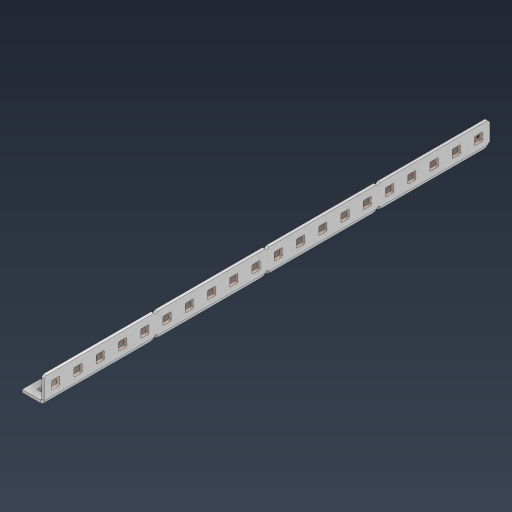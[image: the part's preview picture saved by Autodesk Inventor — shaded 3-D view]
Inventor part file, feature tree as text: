
AUTODESK INVENTOR PART (.ipt)
format: ipt  version: 2024.3 (Build 283343000, 343)  size: 875,008 bytes
history: native  units: in
note: dims shown in document units (in); Inventor stores cm internally (conversion verified against a paired STEP export)
features: other x67, extrude x58, sheet_metal_op x11, pattern_linear x2, mirror x1, chamfer x1, sketch x1
ambient origin geometry x8: Origin, YZ Plane, XZ Plane, XY Plane, X Axis, Y Axis, Z Axis, Center Point
bodies: Solid1 (feature_tree), Body (feature_tree)
feature tree (141):
  sheet_metal_op  "Flanges"
  other  "Flange Pattern Plane"
  other  "Flange Pattern Sketch"
  sheet_metal_op  "Flange Pattern"
  sheet_metal_op  "Body Pattern"
  pattern_linear  "Center Pattern"  Spacing1=10.0in  [1 undecoded]
  other  "Arc Length"
  mirror  "Notch Mirror"
  pattern_linear  "Notch Pattern"  Spacing1=0.0625in  [1 undecoded]
  chamfer  "End Chamfer"
  extrude  "Half Cut"  Depth=0.0625in
  other  "Plate1"
  sketch  "Sketch2"  dims[d0=1.0in d1=10.0in d2=0.0625in d3=0.0625in d4=0.0312in d5=0.125in d6=0.0625in d7=0.5in d8=90.0deg d9=0.0312in d10=0.25in d11=0.0625in d12=0.0625in d16=0.182in d17=0.02in d18=0.0625in d19=0.0in d20=0.25in d21=0.25in d38=7.874in d40=0.5in d41=0.3937in d43=1.0in d46=0.172in d47=1.0in d48=0.0in d49=0.182in d50=0.02in d51=0.25in d52=0.25in d53=0.0625in d54=0.0in d55=0.172in d56=1.0in d57=0.0in d58=0.25in d60=7.874in d62=0.5in d63=0.3937in d65=0.5in d85=0.1473in d86=0.1782in d88=0.04in d89=0.0625in d90=0.0in d91=0.04in d92=0.0491in d95=2.5in d96=0.04in d97=0.25in d98=45.0deg d99=0.25in d100=0.5in d101=0.0in d102=2.497in d106=0.182in d107=0.02in d108=0.5in d109=0.5in d110=0.0625in d111=0.0in d112=0.172in d113=0.5in d114=0.0in d117=0.5in d118=0.5in d119=0.5in]
  other  "Plate2"
  sheet_metal_op  "Bend1"
  sheet_metal_op  "Corner1"
  other  "Srf1"
  other  "Srf2"
  other  "Srf91"
  sheet_metal_op  "Body Pattern Sketch"
  other  "Srf92"
  other  "Srf786"
  other  "Srf823"
  other  "Srf824"
  other  "Srf825"
  other  "Srf826"
  other  "Srf827"
  other  "Srf828"
  other  "Srf829"
  other  "Srf856"
  other  "Srf857"
  other  "Srf858"
  other  "Srf859"
  other  "Srf860"
  other  "Srf861"
  other  "Srf862"
  other  "Srf889"
  other  "Srf890"
  other  "Srf891"
  other  "Srf892"
  other  "Srf893"
  other  "Srf894"
  other  "Srf895"
  other  "Srf896"
  other  "Srf922"
  other  "Srf923"
  other  "Srf924"
  other  "Srf925"
  other  "Srf926"
  other  "Srf959"
  other  "Srf960"
  other  "Srf961"
  other  "Srf962"
  other  "Srf963"
  other  "Srf996"
  other  "Srf997"
  other  "Srf998"
  other  "Srf999"
  other  "Srf1000"
  other  "Srf1143"
  other  "Srf1144"
  other  "Srf1145"
  other  "Srf1146"
  other  "Srf1147"
  other  "Srf1148"
  other  "Srf1199"
  other  "Srf1200"
  other  "Srf1201"
  other  "Srf1202"
  other  "Srf1203"
  other  "Srf1204"
  other  "Srf1255"
  other  "Srf1256"
  other  "Srf1257"
  other  "Srf1258"
  other  "Srf1259"
  other  "Srf1260"
  sheet_metal_op  "Flange Stamp"
  sheet_metal_op  "Flange Circle"
  sheet_metal_op  "Body Stamp"
  sheet_metal_op  "Body Circle"
  other  "Center Stamp"
  other  "Center Circle"
  sheet_metal_op  "Notch"
  extrude  "ExtrusionSrf2"  Depth=0.0312in
  extrude  "ExtrusionSrf92"  Depth=0.5in
  extrude  "ExtrusionSrf823"  Depth=0.0625in
  extrude  "ExtrusionSrf824"  Depth=0.5in TaperAngle=90.0deg
  extrude  "ExtrusionSrf825"  Depth=0.25in
  extrude  "ExtrusionSrf826"  Depth=0.0625in
  extrude  "ExtrusionSrf827"  Depth=0.0625in
  extrude  "ExtrusionSrf828"  Depth=0.182in
  extrude  "ExtrusionSrf829"  Depth=0.02in
  extrude  "ExtrusionSrf856"  Depth=0.0625in
  extrude  "ExtrusionSrf857"  TaperAngle=0.0deg  [1 undecoded]
  extrude  "ExtrusionSrf858"  Depth=0.25in
  extrude  "ExtrusionSrf859"  Depth=0.25in
  extrude  "ExtrusionSrf860"  Depth=0.5in
  extrude  "ExtrusionSrf861"  Depth=0.5in
  extrude  "ExtrusionSrf862"  Depth=1.0in TaperAngle=0.0deg
  extrude  "ExtrusionSrf889"  Depth=0.182in
  extrude  "ExtrusionSrf890"  Depth=0.02in
  extrude  "ExtrusionSrf891"  Depth=0.25in
  extrude  "ExtrusionSrf892"  Depth=0.25in
  extrude  "ExtrusionSrf893"  Depth=0.0625in
  extrude  "ExtrusionSrf894"  TaperAngle=0.0deg  [1 undecoded]
  extrude  "ExtrusionSrf895"  Depth=0.5in
  extrude  "ExtrusionSrf896"  Depth=1.0in TaperAngle=0.0deg
  extrude  "ExtrusionSrf922"  Depth=0.25in
  extrude  "ExtrusionSrf923"  Depth=0.5in
  extrude  "ExtrusionSrf924"  Depth=0.5in
  extrude  "ExtrusionSrf925"  Depth=0.5in
  extrude  "ExtrusionSrf926"  Depth=0.5in
  extrude  "ExtrusionSrf959"  Depth=0.5in
  extrude  "ExtrusionSrf960"  Depth=0.0625in
  extrude  "ExtrusionSrf961"  TaperAngle=0.0deg  [1 undecoded]
  extrude  "ExtrusionSrf962"  Depth=0.5in
  extrude  "ExtrusionSrf963"  Depth=0.5in
  extrude  "ExtrusionSrf996"  Depth=2.5in
  extrude  "ExtrusionSrf997"  Depth=0.25in TaperAngle=45.0deg
  extrude  "ExtrusionSrf998"  Depth=0.25in
  extrude  "ExtrusionSrf999"  Depth=0.5in TaperAngle=0.0deg
  extrude  "ExtrusionSrf1000"  Depth=0.5in
  extrude  "ExtrusionSrf1143"  Depth=0.182in
  extrude  "ExtrusionSrf1144"  Depth=0.02in
  extrude  "ExtrusionSrf1145"  Depth=0.5in
  extrude  "ExtrusionSrf1146"  Depth=0.5in
  extrude  "ExtrusionSrf1147"  Depth=0.0625in
  extrude  "ExtrusionSrf1148"  TaperAngle=0.0deg  [1 undecoded]
  extrude  "ExtrusionSrf1199"  Depth=0.5in
  extrude  "ExtrusionSrf1200"  Depth=0.5in TaperAngle=0.0deg
  extrude  "ExtrusionSrf1201"  Depth=0.5in
  extrude  "ExtrusionSrf1202"  Depth=0.5in
  extrude  "ExtrusionSrf1203"  Depth=0.5in
  extrude  "ExtrusionSrf1204"  [1 undecoded]
  extrude  "ExtrusionSrf1255"  [1 undecoded]
  extrude  "ExtrusionSrf1256"  [1 undecoded]
  extrude  "ExtrusionSrf1257"  [1 undecoded]
  extrude  "ExtrusionSrf1258"  [1 undecoded]
  extrude  "ExtrusionSrf1259"  [1 undecoded]
  extrude  "ExtrusionSrf1260"  [1 undecoded]
note: 13 required parameter values undecoded (feature->parameter linkage not recoverable at this tier; creation-order binding heuristic only, values carry confidence <= 0.55)
